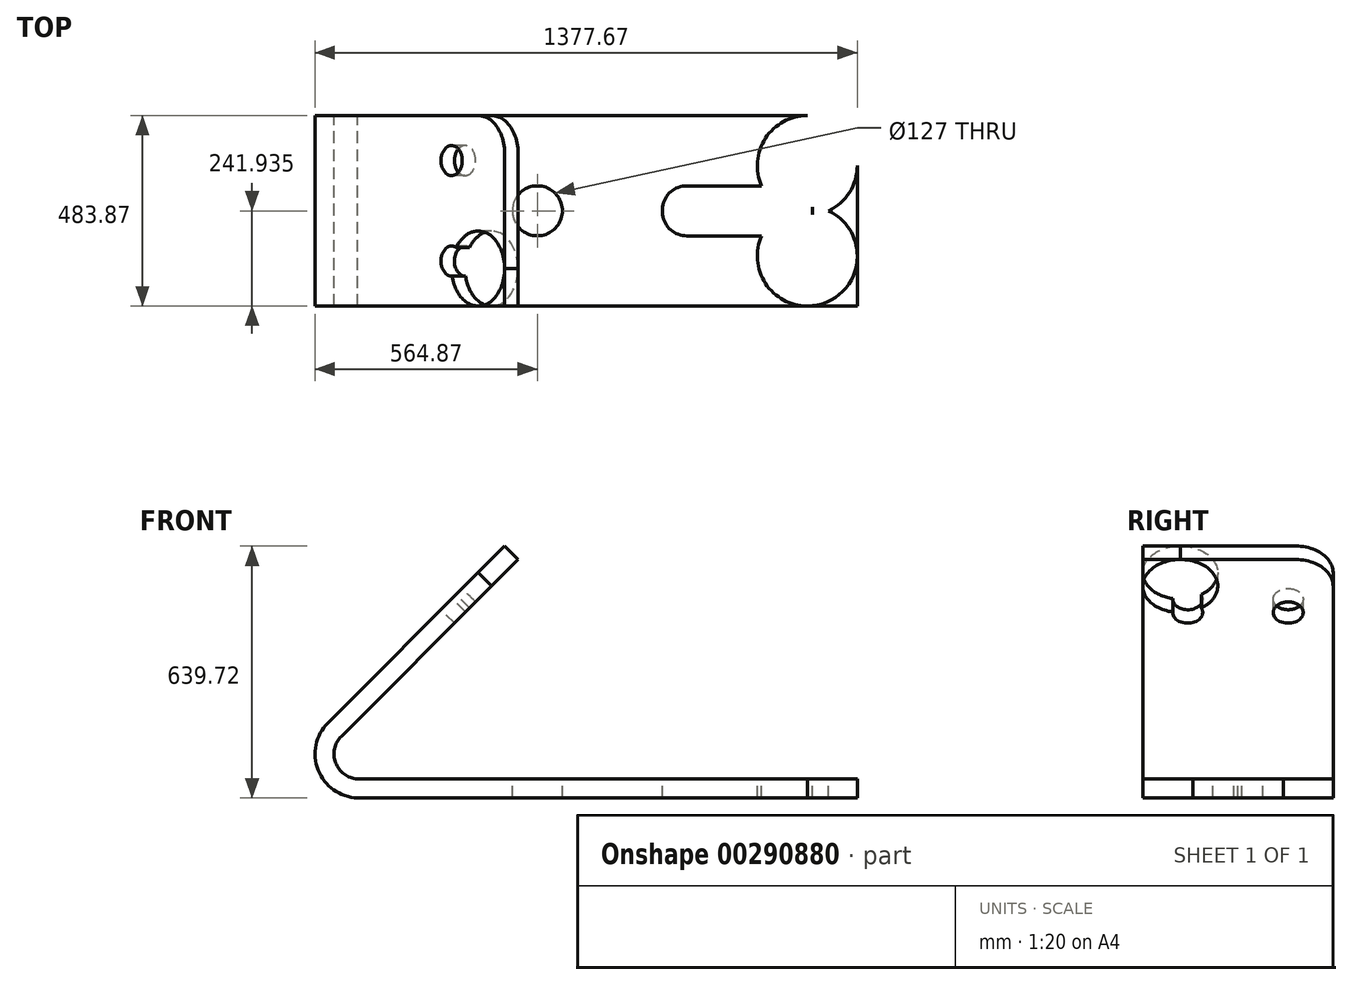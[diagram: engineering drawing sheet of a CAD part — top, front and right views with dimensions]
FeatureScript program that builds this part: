
annotation { "Feature Type Name" : "Feature", "Feature Type Description" : "" }
export const myFeature = defineFeature(function(context is Context, id is Id, definition is map)
    precondition{}
    {
        {
            var Q0;
            Q0=qCreatedBy(makeId("Front.planeOp"),FACE);
            var sketch = newSketch(context, id + "F0", { "sketchPlane" : qUnion([Q0])});
            skLineSegment(sketch, "E0.bottom", {"start": v(635, 24.13) * mm, "end": v(-635, 24.13) * mm});
            skLineSegment(sketch, "E0.top", {"start": v(635, -24.13) * mm, "end": v(-635, -24.13) * mm});
            skLineSegment(sketch, "E0.left", {"start": v(635, 24.13) * mm, "end": v(635, -24.13) * mm});
            skLineSegment(sketch, "E0.right", {"start": v(-635, 24.13) * mm, "end": v(-635, -24.13) * mm});
            skPoint(sketch, "E0.middle", {"position": v(0, 0) * mm});
            skLineSegment(sketch, "E1.bottom", {"start": v(-675.81, 132.46) * mm, "end": v(-709.94, 166.58) * mm});
            skLineSegment(sketch, "E1.top", {"start": v(-226.8, 581.47) * mm, "end": v(-260.93, 615.6) * mm});
            skLineSegment(sketch, "E1.left", {"start": v(-675.81, 132.46) * mm, "end": v(-226.8, 581.47) * mm});
            skLineSegment(sketch, "E1.right", {"start": v(-709.94, 166.58) * mm, "end": v(-260.93, 615.6) * mm});
            skPoint(sketch, "E1.middle", {"position": v(-468.37, 374.03) * mm});
            skArc(sketch, "E2", {"start": v(-709.94, 166.58) * mm, "mid": v(-734.93, 46.68) * mm, "end": v(-635, -24.13) * mm});
            skArc(sketch, "E3", {"start": v(-675.81, 132.46) * mm, "mid": v(-690.34, 65.13) * mm, "end": v(-635, 24.13) * mm});
            skSolve(sketch);
        }
        {
            var Q0;
            Q0=makeQuery(id+"F0.imprint","IMPRINT",FACE,{"disambiguationData":[TD([[makeQuery(id+"F0.imprint","IMPRINT",EDGE,{"derivedFrom":sQuery(id+"F0.wireOp",EDGE,"E1.bottom")}),-1.0]])]});
            var Q1;
            Q1=makeQuery(id+"F0.imprint","IMPRINT",FACE,{"disambiguationData":[TD([[makeQuery(id+"F0.imprint","IMPRINT",EDGE,{"derivedFrom":sQuery(id+"F0.wireOp",EDGE,"E0.right")}),-1.0]])]});
            var Q2;
            Q2=makeQuery(id+"F0.imprint","IMPRINT",FACE,{"disambiguationData":[TD([[makeQuery(id+"F0.imprint","IMPRINT",EDGE,{"derivedFrom":sQuery(id+"F0.wireOp",EDGE,"E0.bottom")}),1.0]])]});
            extrude(context, id + "F1", {"entities" : qUnion([Q0, Q1, Q2]), "depth" : 483.87 * mm});
        }
        {
            var Q0;
            Q0=makeQuery(id+"F1.opExtrude","SWEPT_FACE",FACE,{"disambiguationData":[OSD([sQuery(id+"F0.wireOp",EDGE,"E1.right")])]});
            var sketch = newSketch(context, id + "F2", { "sketchPlane" : qUnion([Q0])});
            skCircle(sketch, "E4", {"center": v(95.25, 155.54) * mm, "radius": 95.25 * mm});
            skLineSegment(sketch, "E5", {"start": v(241.94, 250.79) * mm, "end": v(241.94, -384.21) * mm, "construction": true});
            skCircle(sketch, "E6.MirrorC", {"center": v(388.62, 155.54) * mm, "radius": 95.25 * mm});
            skLineSegment(sketch, "E7", {"start": v(369.57, -384.21) * mm, "end": v(369.57, 60.29) * mm, "construction": true});
            skCircle(sketch, "E8", {"center": v(369.57, 60.29) * mm, "radius": 38.1 * mm});
            skCircle(sketch, "E9.MirrorC", {"center": v(114.3, 60.29) * mm, "radius": 38.1 * mm});
            skSolve(sketch);
        }
        {
            var Q0;
            {var subQ0=sQuery(id+"F2.wireOp",EDGE,"E6.MirrorC");var subQ1=sQuery(id+"F0.wireOp",EDGE,"E1.right");var subQ2=makeQuery(id+"F1.opExtrude","CAP_EDGE",EDGE,{"disambiguationData":[OSD([subQ1])],"isStart":false});var subQ3=makeQuery(id+"F2.imprint","INTERSECT",VERTEX,{"derivedFrom":[subQ2,subQ0]});Q0=makeQuery(id+"F2.imprint","IMPRINT",FACE,{"disambiguationData":[TD([[makeQuery(id+"F2.imprint","IMPRINT",EDGE,{"disambiguationData":[TD([[subQ3,1.0]])],"derivedFrom":subQ0}),1.0]])]});}
            var Q1;
            {var subQ0=sQuery(id+"F2.wireOp",EDGE,"E4");var subQ1=sQuery(id+"F0.wireOp",EDGE,"E1.right");var subQ2=makeQuery(id+"F1.opExtrude","CAP_EDGE",EDGE,{"disambiguationData":[OSD([subQ1])],"isStart":true});var subQ3=makeQuery(id+"F2.imprint","INTERSECT",VERTEX,{"derivedFrom":[subQ2,subQ0]});Q1=makeQuery(id+"F2.imprint","IMPRINT",FACE,{"disambiguationData":[TD([[makeQuery(id+"F2.imprint","IMPRINT",EDGE,{"disambiguationData":[TD([[subQ3,1.0]])],"derivedFrom":subQ0}),-1.0]])]});}
            var Q2;
            {var subQ0=sQuery(id+"F2.wireOp",EDGE,"E9.MirrorC");var subQ1=sQuery(id+"F2.wireOp",EDGE,"E4");var subQ2=makeQuery(id+"F2.imprint","INTERSECT",VERTEX,{"disambiguationData":[OD(0.0)],"derivedFrom":[subQ1,subQ0]});Q2=makeQuery(id+"F2.imprint","IMPRINT",FACE,{"disambiguationData":[TD([[makeQuery(id+"F2.imprint","IMPRINT",EDGE,{"disambiguationData":[TD([[subQ2,-1.0]])],"derivedFrom":subQ1}),-1.0]])]});}
            var Q3;
            {var subQ0=sQuery(id+"F2.wireOp",EDGE,"E9.MirrorC");var subQ1=sQuery(id+"F2.wireOp",EDGE,"E4");var subQ2=makeQuery(id+"F2.imprint","INTERSECT",VERTEX,{"disambiguationData":[OD(0.0)],"derivedFrom":[subQ1,subQ0]});Q3=makeQuery(id+"F2.imprint","IMPRINT",FACE,{"disambiguationData":[TD([[makeQuery(id+"F2.imprint","IMPRINT",EDGE,{"disambiguationData":[TD([[subQ2,-1.0]])],"derivedFrom":subQ1}),1.0]])]});}
            var Q4;
            {var subQ0=sQuery(id+"F2.wireOp",EDGE,"E8");var subQ1=sQuery(id+"F2.wireOp",EDGE,"E6.MirrorC");var subQ2=makeQuery(id+"F2.imprint","INTERSECT",VERTEX,{"disambiguationData":[OD(0.0)],"derivedFrom":[subQ1,subQ0]});Q4=makeQuery(id+"F2.imprint","IMPRINT",FACE,{"disambiguationData":[TD([[makeQuery(id+"F2.imprint","IMPRINT",EDGE,{"disambiguationData":[TD([[subQ2,-1.0]])],"derivedFrom":subQ1}),1.0]])]});}
            var Q5;
            {var subQ0=sQuery(id+"F2.wireOp",EDGE,"E8");var subQ1=sQuery(id+"F2.wireOp",EDGE,"E6.MirrorC");var subQ2=makeQuery(id+"F2.imprint","INTERSECT",VERTEX,{"disambiguationData":[OD(0.0)],"derivedFrom":[subQ1,subQ0]});Q5=makeQuery(id+"F2.imprint","IMPRINT",FACE,{"disambiguationData":[TD([[makeQuery(id+"F2.imprint","IMPRINT",EDGE,{"disambiguationData":[TD([[subQ2,-1.0]])],"derivedFrom":subQ1}),-1.0]])]});}
            extrude(context, id + "F3", {"entities" : qUnion([Q0, Q1, Q2, Q3, Q4, Q5]), "operationType" : NewBodyOperationType.REMOVE, "oppositeDirection" : true, "depth" : 61.47 * mm});
        }
        {
            var Q0;
            Q0=makeQuery(id+"F1.opExtrude","SWEPT_FACE",FACE,{"disambiguationData":[OSD([sQuery(id+"F0.wireOp",EDGE,"E0.bottom")])]});
            var sketch = newSketch(context, id + "F4", { "sketchPlane" : qUnion([Q0])});
            skLineSegment(sketch, "E10", {"start": v(635, -241.94) * mm, "end": v(-798.04, -241.94) * mm, "construction": true});
            skLineSegment(sketch, "E11.bottom", {"start": v(457.99, -178.44) * mm, "end": v(202.41, -178.44) * mm});
            skLineSegment(sketch, "E11.top", {"start": v(457.99, -305.44) * mm, "end": v(202.41, -305.44) * mm});
            skLineSegment(sketch, "E11.left", {"start": v(520.7, -231.96) * mm, "end": v(520.7, -251.9) * mm});
            skLineSegment(sketch, "E11.right", {"start": v(139.7, -231.96) * mm, "end": v(139.7, -251.9) * mm});
            skPoint(sketch, "E11.middle", {"position": v(330.2, -241.94) * mm});
            skCircle(sketch, "E12", {"center": v(-177.8, -241.94) * mm, "radius": 63.5 * mm});
            skArc(sketch, "E13", {"start": v(457.99, -305.44) * mm, "mid": v(521.49, -241.94) * mm, "end": v(457.99, -178.44) * mm});
            skLineSegment(sketch, "E14", {"start": v(330.2, -178.44) * mm, "end": v(330.2, -305.44) * mm, "construction": true});
            skArc(sketch, "E15.MirrorC", {"start": v(202.41, -305.44) * mm, "mid": v(138.91, -241.94) * mm, "end": v(202.41, -178.44) * mm});
            skPoint(sketch, "E16.orphan", {"position": v(520.7, -178.44) * mm});
            skPoint(sketch, "E17.orphan", {"position": v(520.7, -305.44) * mm});
            skPoint(sketch, "E18.orphan", {"position": v(139.7, -305.44) * mm});
            skPoint(sketch, "E19.orphan", {"position": v(139.7, -178.44) * mm});
            skArc(sketch, "E20", {"start": v(562.03, -241.94) * mm, "mid": v(552.4, -8.02) * mm, "end": v(391.88, -178.44) * mm});
            skArc(sketch, "E21.MirrorCS", {"start": v(562.03, -241.94) * mm, "mid": v(552.4, -475.85) * mm, "end": v(391.88, -305.43) * mm});
            skSolve(sketch);
        }
        {
            var Q0;
            {var subQ11=sQuery(id+"F4.wireOp",EDGE,"E11.left");Q0=makeQuery(id+"F4.imprint","IMPRINT",FACE,{"disambiguationData":[TD([[makeQuery(id+"F4.imprint","IMPRINT",EDGE,{"derivedFrom":subQ11}),-1.0]])]});}
            var Q1;
            Q1=makeQuery(id+"F4.imprint","IMPRINT",FACE,{"disambiguationData":[TD([[makeQuery(id+"F4.imprint","IMPRINT",EDGE,{"derivedFrom":sQuery(id+"F4.wireOp",EDGE,"E12")}),1.0]])]});
            var Q2;
            {var subQ0=sQuery(id+"F4.wireOp",EDGE,"E20");var subQ1=sQuery(id+"F0.wireOp",EDGE,"E0.bottom");var subQ4=makeQuery(id+"F1.opExtrude","CAP_EDGE",EDGE,{"disambiguationData":[OSD([subQ1])],"isStart":true});var subQ5=makeQuery(id+"F4.imprint","INTERSECT",VERTEX,{"derivedFrom":[subQ4,subQ0]});Q2=makeQuery(id+"F4.imprint","IMPRINT",FACE,{"disambiguationData":[TD([[makeQuery(id+"F4.imprint","IMPRINT",EDGE,{"disambiguationData":[TD([[subQ5,1.0]])],"derivedFrom":subQ0}),-1.0]])]});}
            var Q3;
            {var subQ0=sQuery(id+"F4.wireOp",EDGE,"E21.MirrorCS");var subQ1=sQuery(id+"F0.wireOp",EDGE,"E0.bottom");var subQ4=makeQuery(id+"F1.opExtrude","CAP_EDGE",EDGE,{"disambiguationData":[OSD([subQ1])],"isStart":false});var subQ5=makeQuery(id+"F4.imprint","INTERSECT",VERTEX,{"derivedFrom":[subQ4,subQ0]});Q3=makeQuery(id+"F4.imprint","IMPRINT",FACE,{"disambiguationData":[TD([[makeQuery(id+"F4.imprint","IMPRINT",EDGE,{"disambiguationData":[TD([[subQ5,1.0]])],"derivedFrom":subQ0}),1.0]])]});}
            extrude(context, id + "F5", {"entities" : qUnion([Q0, Q1, Q2, Q3]), "operationType" : NewBodyOperationType.REMOVE, "endBound" : BoundingType.THROUGH_ALL, "oppositeDirection" : true, "depth" : 25.4 * mm});
        }
    });
